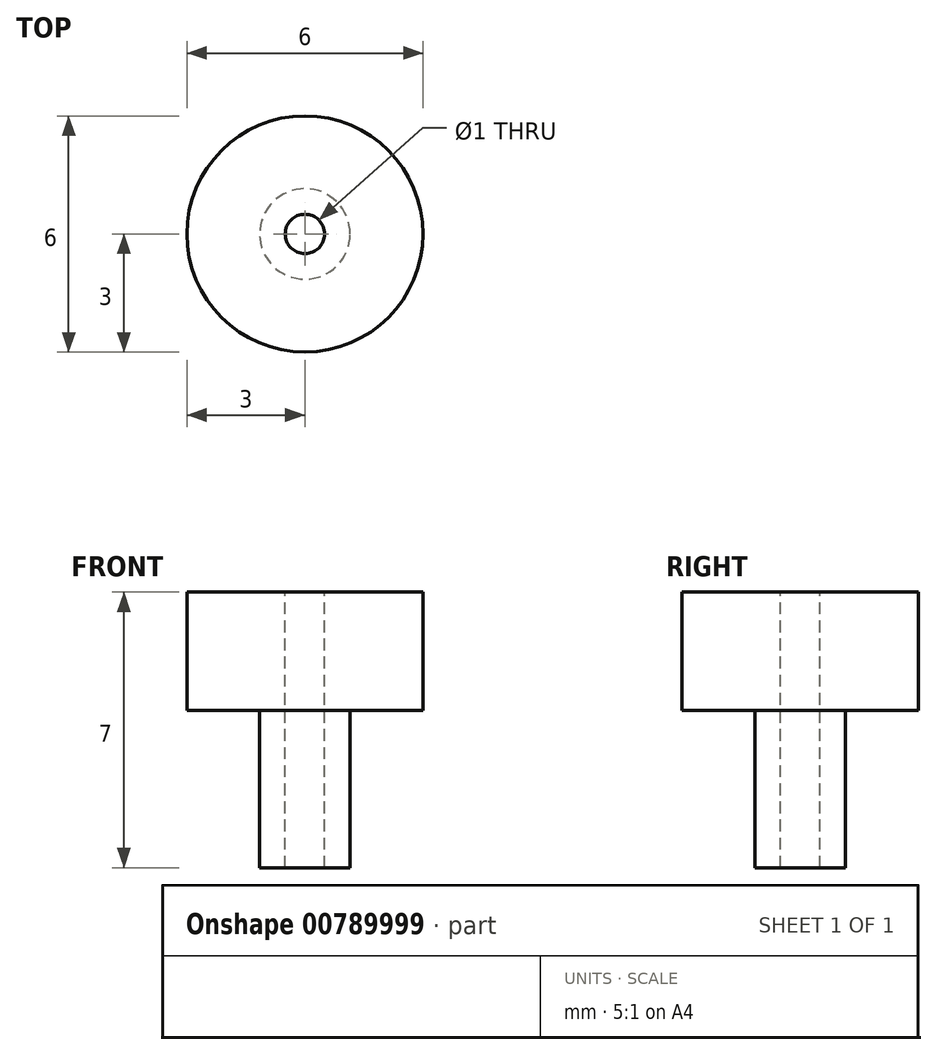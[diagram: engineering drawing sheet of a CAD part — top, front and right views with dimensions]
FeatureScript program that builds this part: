
annotation { "Feature Type Name" : "Feature", "Feature Type Description" : "" }
export const myFeature = defineFeature(function(context is Context, id is Id, definition is map)
    precondition{}
    {
        {
            var Q0;
            Q0=qCreatedBy(makeId("Top.planeOp"),FACE);
            var sketch = newSketch(context, id + "F0", { "sketchPlane" : qUnion([Q0])});
            skCircle(sketch, "E0", {"center": v(0, 0) * mm, "radius": 3 * mm});
            skSolve(sketch);
        }
        {
            var Q0;
            Q0 = qSketchRegion(id + "F0", true);
            extrude(context, id + "F1", {"entities" : qUnion([Q0]), "depth" : 7 * mm, "offsetDistance" : 25 * mm});
        }
        {
            var Q0;
            Q0=makeQuery(id+"F1.opExtrude","CAP_FACE",FACE,{"disambiguationData":[OSD([sQuery(id+"F0.wireOp",EDGE,"E0")])],"isStart":true});
            var sketch = newSketch(context, id + "F2", { "sketchPlane" : qUnion([Q0])});
            skCircle(sketch, "E1", {"center": v(0, 0) * mm, "radius": 3 * mm});
            skCircle(sketch, "E2", {"center": v(0, 0) * mm, "radius": 1.15 * mm});
            skSolve(sketch);
        }
        {
            var Q0;
            Q0 = qSketchRegion(id + "F2", true);
            extrude(context, id + "F3", {"entities" : qUnion([Q0]), "operationType" : NewBodyOperationType.REMOVE, "oppositeDirection" : true, "depth" : 4 * mm, "offsetDistance" : 25 * mm});
        }
        {
            var Q0;
            Q0=makeQuery(id+"F1.opExtrude","CAP_FACE",FACE,{"disambiguationData":[OSD([sQuery(id+"F0.wireOp",EDGE,"E0")])],"isStart":false});
            var sketch = newSketch(context, id + "F4", { "sketchPlane" : qUnion([Q0])});
            skCircle(sketch, "E3", {"center": v(0, 0) * mm, "radius": 0.5 * mm});
            skSolve(sketch);
        }
        {
            var Q0;
            Q0 = qSketchRegion(id + "F4", true);
            extrude(context, id + "F5", {"entities" : qUnion([Q0]), "operationType" : NewBodyOperationType.REMOVE, "oppositeDirection" : true, "depth" : 25 * mm, "offsetDistance" : 25 * mm});
        }
    });
